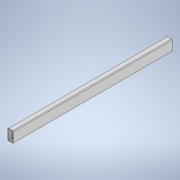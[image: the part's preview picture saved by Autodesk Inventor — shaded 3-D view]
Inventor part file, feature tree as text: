
AUTODESK INVENTOR PART (.ipt)
format: ipt  version: 2020 (Build 240168000, 168)  size: 127,488 bytes
history: native  units: in
note: dims shown in document units (in); Inventor stores cm internally (conversion verified against a paired STEP export)
features: extrude x1, sketch x1
ambient origin geometry x8: Origin, YZ Plane, XZ Plane, XY Plane, X Axis, Y Axis, Z Axis, Center Point
bodies: Solid1 (feature_tree)
feature tree (2):
  extrude  "Extrusion1"  Depth=1.0in
  sketch  "Sketch1"  dims[d0=2.0in d1=1.0in d2=0.125in d3=0.125in d4=0.125in d5=0.125in d6=0.125in d7=0.125in d8=0.125in d9=0.125in d10=0.125in d11=29.0in d12=0.0in]
